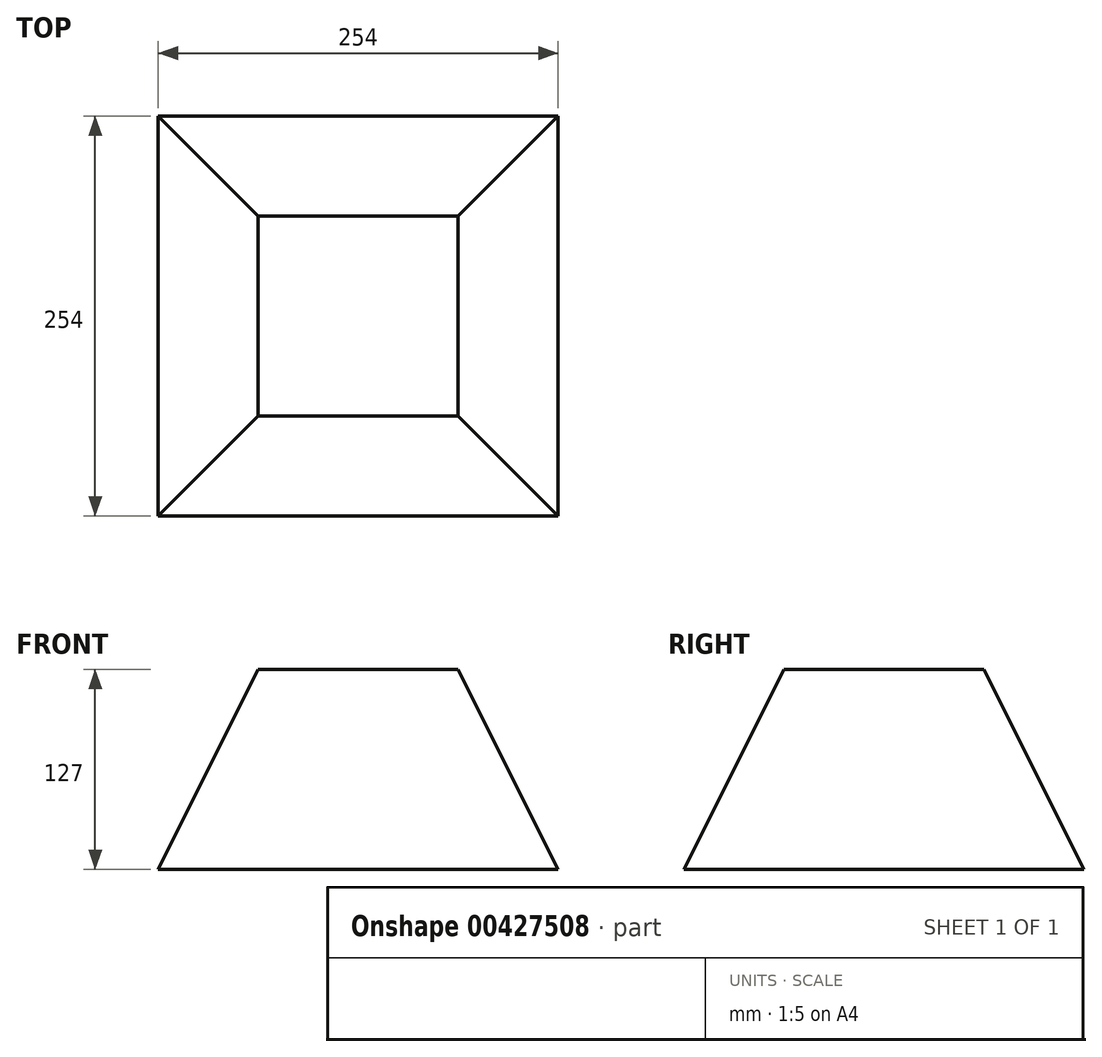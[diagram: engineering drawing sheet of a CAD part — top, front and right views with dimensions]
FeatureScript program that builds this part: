
annotation { "Feature Type Name" : "Feature", "Feature Type Description" : "" }
export const myFeature = defineFeature(function(context is Context, id is Id, definition is map)
    precondition{}
    {
        {
            var Q0;
            Q0=qCreatedBy(makeId("Top.planeOp"),FACE);
            var sketch = newSketch(context, id + "F0", { "sketchPlane" : qUnion([Q0])});
            skLineSegment(sketch, "E0.bottom", {"start": v(127, 127) * mm, "end": v(-127, 127) * mm});
            skLineSegment(sketch, "E0.top", {"start": v(127, -127) * mm, "end": v(-127, -127) * mm});
            skLineSegment(sketch, "E0.left", {"start": v(127, 127) * mm, "end": v(127, -127) * mm});
            skLineSegment(sketch, "E0.right", {"start": v(-127, 127) * mm, "end": v(-127, -127) * mm});
            skPoint(sketch, "E0.middle", {"position": v(0, 0) * mm});
            skSolve(sketch);
        }
        {
            var Q0;
            Q0=makeQuery(id+"F0.imprint","IMPRINT",FACE,{"disambiguationData":[TD([[makeQuery(id+"F0.imprint","IMPRINT",EDGE,{"derivedFrom":sQuery(id+"F0.wireOp",EDGE,"E0.bottom")}),1.0]])]});
            cPlane(context, id + "F1", {"entities" : qUnion([Q0]), "cplaneType" : CPlaneType.OFFSET, "offset" : 127 * mm, "width" : 152.4 * mm, "height" : 152.4 * mm});
        }
        {
            var Q0;
            Q0=qCreatedBy(id+"F1.planeOp",FACE);
            var sketch = newSketch(context, id + "F2", { "sketchPlane" : qUnion([Q0])});
            skLineSegment(sketch, "E1.bottom", {"start": v(63.5, 63.5) * mm, "end": v(-63.5, 63.5) * mm});
            skLineSegment(sketch, "E1.top", {"start": v(63.5, -63.5) * mm, "end": v(-63.5, -63.5) * mm});
            skLineSegment(sketch, "E1.left", {"start": v(63.5, 63.5) * mm, "end": v(63.5, -63.5) * mm});
            skLineSegment(sketch, "E1.right", {"start": v(-63.5, 63.5) * mm, "end": v(-63.5, -63.5) * mm});
            skPoint(sketch, "E1.middle", {"position": v(0, 0) * mm});
            skSolve(sketch);
        }
        {
            var Q0;
            Q0=makeQuery(id+"F2.imprint","IMPRINT",FACE,{"disambiguationData":[TD([[makeQuery(id+"F2.imprint","IMPRINT",EDGE,{"derivedFrom":sQuery(id+"F2.wireOp",EDGE,"E1.bottom")}),1.0]])]});
            var Q1;
            Q1=makeQuery(id+"F0.imprint","IMPRINT",FACE,{"disambiguationData":[TD([[makeQuery(id+"F0.imprint","IMPRINT",EDGE,{"derivedFrom":sQuery(id+"F0.wireOp",EDGE,"E0.bottom")}),1.0]])]});
            loft(context, id + "F3", {"sheetProfilesArray" : [{ "sheetProfileEntities" : qUnion([Q0]) }, { "sheetProfileEntities" : qUnion([Q1]) }]});
        }
    });
